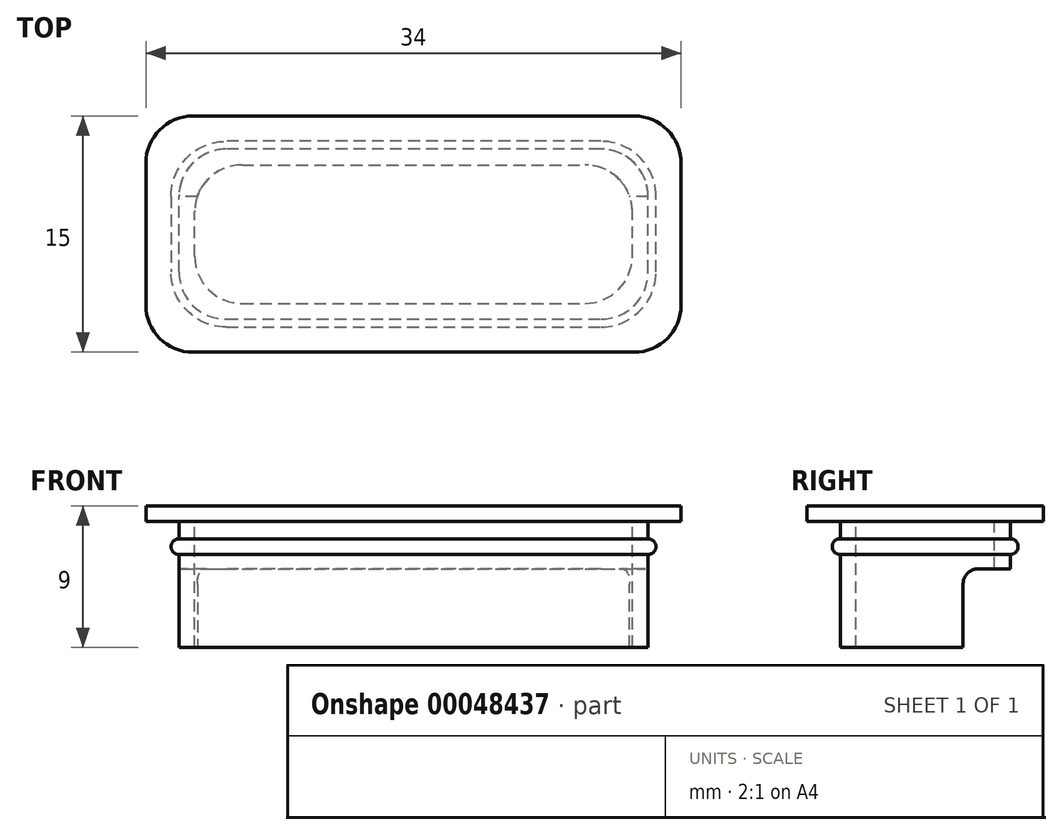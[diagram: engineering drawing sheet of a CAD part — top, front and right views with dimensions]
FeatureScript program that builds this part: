
annotation { "Feature Type Name" : "Feature", "Feature Type Description" : "" }
export const myFeature = defineFeature(function(context is Context, id is Id, definition is map)
    precondition{}
    {
        {
            var Q0;
            Q0=qCreatedBy(makeId("Top.planeOp"),FACE);
            var sketch = newSketch(context, id + "F0", { "sketchPlane" : qUnion([Q0])});
            skLineSegment(sketch, "E0.rect.bottom", {"start": v(17, -7.5) * mm, "end": v(-17, -7.5) * mm});
            skLineSegment(sketch, "E0.rect.top", {"start": v(17, 7.5) * mm, "end": v(-17, 7.5) * mm});
            skLineSegment(sketch, "E0.rect.left", {"start": v(17, -7.5) * mm, "end": v(17, 7.5) * mm});
            skLineSegment(sketch, "E0.rect.right", {"start": v(-17, -7.5) * mm, "end": v(-17, 7.5) * mm});
            skPoint(sketch, "E0.rect.middle", {"position": v(0, 0) * mm});
            skSolve(sketch);
        }
        {
            var Q0;
            Q0=makeQuery(id+"F0.imprint","IMPRINT",FACE,{"disambiguationData":[TD([[makeQuery(id+"F0.imprint","IMPRINT",EDGE,{"derivedFrom":sQuery(id+"F0.wireOp",EDGE,"E0.rect.bottom")}),-1.0]])]});
            extrude(context, id + "F1", {"entities" : qUnion([Q0]), "endBound" : BoundingType.SYMMETRIC, "depth" : 1 * mm});
        }
        {
            var Q0;
            Q0=makeQuery(id+"F1.opExtrude","CAP_FACE",FACE,{"disambiguationData":[OSD([sQuery(id+"F0.wireOp",EDGE,"E0.rect.bottom"),sQuery(id+"F0.wireOp",EDGE,"E0.rect.top"),sQuery(id+"F0.wireOp",EDGE,"E0.rect.left"),sQuery(id+"F0.wireOp",EDGE,"E0.rect.right")])],"isStart":true});
            var sketch = newSketch(context, id + "F2", { "sketchPlane" : qUnion([Q0])});
            skLineSegment(sketch, "E1.rect.bottom", {"start": v(-14.9, 5.4) * mm, "end": v(14.9, 5.4) * mm});
            skLineSegment(sketch, "E1.rect.top", {"start": v(-14.9, -5.4) * mm, "end": v(14.9, -5.4) * mm});
            skLineSegment(sketch, "E1.rect.left", {"start": v(-14.9, 5.4) * mm, "end": v(-14.9, -5.4) * mm});
            skLineSegment(sketch, "E1.rect.right", {"start": v(14.9, 5.4) * mm, "end": v(14.9, -5.4) * mm});
            skPoint(sketch, "E1.rect.middle", {"position": v(0, 0) * mm});
            skSolve(sketch);
        }
        {
            var Q0;
            Q0=makeQuery(id+"F2.imprint","IMPRINT",FACE,{"disambiguationData":[TD([[makeQuery(id+"F2.imprint","IMPRINT",EDGE,{"derivedFrom":sQuery(id+"F2.wireOp",EDGE,"E1.rect.bottom")}),-1.0]])]});
            extrude(context, id + "F3", {"entities" : qUnion([Q0]), "operationType" : NewBodyOperationType.ADD, "depth" : 8 * mm});
        }
        {
            var Q0;
            Q0=makeQuery(id+"F3.opExtrude","CAP_FACE",FACE,{"disambiguationData":[OSD([sQuery(id+"F2.wireOp",EDGE,"E1.rect.bottom"),sQuery(id+"F2.wireOp",EDGE,"E1.rect.top"),sQuery(id+"F2.wireOp",EDGE,"E1.rect.left"),sQuery(id+"F2.wireOp",EDGE,"E1.rect.right")])],"isStart":false});
            shell(context, id + "F4", {"entities" : qUnion([Q0]), "thickness" : 1 * mm});
        }
        {
            var Q0;
            Q0=makeQuery(id+"F1.opExtrude","SWEPT_EDGE",EDGE,{"disambiguationData":[OSD([sQuery(id+"F0.wireOp",EDGE,"E0.rect.bottom"),sQuery(id+"F0.wireOp",EDGE,"E0.rect.right")])]});
            var Q1;
            Q1=makeQuery(id+"F1.opExtrude","SWEPT_EDGE",EDGE,{"disambiguationData":[OSD([sQuery(id+"F0.wireOp",EDGE,"E0.rect.top"),sQuery(id+"F0.wireOp",EDGE,"E0.rect.right")])]});
            var Q2;
            Q2=makeQuery(id+"F1.opExtrude","SWEPT_EDGE",EDGE,{"disambiguationData":[OSD([sQuery(id+"F0.wireOp",EDGE,"E0.rect.top"),sQuery(id+"F0.wireOp",EDGE,"E0.rect.left")])]});
            var Q3;
            Q3=makeQuery(id+"F1.opExtrude","SWEPT_EDGE",EDGE,{"disambiguationData":[OSD([sQuery(id+"F0.wireOp",EDGE,"E0.rect.bottom"),sQuery(id+"F0.wireOp",EDGE,"E0.rect.left")])]});
            var Q4;
            Q4=makeQuery(id+"F3.opExtrude","SWEPT_EDGE",EDGE,{"disambiguationData":[OSD([sQuery(id+"F2.wireOp",EDGE,"E1.rect.top"),sQuery(id+"F2.wireOp",EDGE,"E1.rect.right")])]});
            var Q5;
            Q5=makeQuery(id+"F3.opExtrude","SWEPT_EDGE",EDGE,{"disambiguationData":[OSD([sQuery(id+"F2.wireOp",EDGE,"E1.rect.top"),sQuery(id+"F2.wireOp",EDGE,"E1.rect.left")])]});
            var Q6;
            Q6=makeQuery(id+"F3.opExtrude","SWEPT_EDGE",EDGE,{"disambiguationData":[OSD([sQuery(id+"F2.wireOp",EDGE,"E1.rect.bottom"),sQuery(id+"F2.wireOp",EDGE,"E1.rect.left")])]});
            var Q7;
            Q7=makeQuery(id+"F3.opExtrude","SWEPT_EDGE",EDGE,{"disambiguationData":[OSD([sQuery(id+"F2.wireOp",EDGE,"E1.rect.bottom"),sQuery(id+"F2.wireOp",EDGE,"E1.rect.right")])]});
            var Q8;
            Q8=makeQuery(id+"F4.opShell","OFFSET_EDGE",EDGE,{"disambiguationData":[OSD([sQuery(id+"F2.wireOp",EDGE,"E1.rect.bottom"),sQuery(id+"F2.wireOp",EDGE,"E1.rect.left")])]});
            var Q9;
            Q9=makeQuery(id+"F4.opShell","OFFSET_EDGE",EDGE,{"disambiguationData":[OSD([sQuery(id+"F2.wireOp",EDGE,"E1.rect.top"),sQuery(id+"F2.wireOp",EDGE,"E1.rect.left")])]});
            var Q10;
            Q10=makeQuery(id+"F4.opShell","OFFSET_EDGE",EDGE,{"disambiguationData":[OSD([sQuery(id+"F2.wireOp",EDGE,"E1.rect.top"),sQuery(id+"F2.wireOp",EDGE,"E1.rect.right")])]});
            var Q11;
            Q11=makeQuery(id+"F4.opShell","OFFSET_EDGE",EDGE,{"disambiguationData":[OSD([sQuery(id+"F2.wireOp",EDGE,"E1.rect.bottom"),sQuery(id+"F2.wireOp",EDGE,"E1.rect.right")])]});
            fillet(context, id + "F5", {"entities" : qUnion([Q0, Q1, Q2, Q3, Q4, Q5, Q6, Q7, Q8, Q9, Q10, Q11]), "radius" : 3 * mm, "tangentPropagation" : true, "allowEdgeOverflow" : false});
        }
        {
            var Q0;
            Q0=makeQuery(id+"F1.opExtrude","CAP_FACE",FACE,{"disambiguationData":[OSD([sQuery(id+"F0.wireOp",EDGE,"E0.rect.bottom"),sQuery(id+"F0.wireOp",EDGE,"E0.rect.top"),sQuery(id+"F0.wireOp",EDGE,"E0.rect.left"),sQuery(id+"F0.wireOp",EDGE,"E0.rect.right")])],"isStart":true});
            cPlane(context, id + "F6", {"entities" : qUnion([Q0]), "cplaneType" : CPlaneType.OFFSET, "offset" : 1.1 * mm, "width" : 150 * mm, "height" : 150 * mm});
        }
        {
            var Q0;
            Q0=qCreatedBy(id+"F6.planeOp",FACE);
            var sketch = newSketch(context, id + "F7", { "sketchPlane" : qUnion([Q0])});
            skLineSegment(sketch, "E2.rect.bottom", {"start": v(-11.9, 5.4) * mm, "end": v(11.9, 5.4) * mm});
            skLineSegment(sketch, "E2.rect.top", {"start": v(-11.9, -5.4) * mm, "end": v(11.9, -5.4) * mm});
            skLineSegment(sketch, "E2.rect.left", {"start": v(-14.9, 2.4) * mm, "end": v(-14.9, -2.4) * mm});
            skLineSegment(sketch, "E2.rect.right", {"start": v(14.9, 2.4) * mm, "end": v(14.9, -2.4) * mm});
            skPoint(sketch, "E2.rect.middle", {"position": v(0, 0) * mm});
            skPoint(sketch, "E3.visualSharp", {"position": v(-14.9, -5.4) * mm});
            skArc(sketch, "E3.filletArc", {"start": v(-14.9, -2.4) * mm, "mid": v(-14.02, -4.52) * mm, "end": v(-11.9, -5.4) * mm});
            skPoint(sketch, "E4.visualSharp", {"position": v(-14.9, 5.4) * mm});
            skArc(sketch, "E4.filletArc", {"start": v(-11.9, 5.4) * mm, "mid": v(-14.02, 4.52) * mm, "end": v(-14.9, 2.4) * mm});
            skPoint(sketch, "E5.visualSharp", {"position": v(14.9, 5.4) * mm});
            skArc(sketch, "E5.filletArc", {"start": v(14.9, 2.4) * mm, "mid": v(14.02, 4.52) * mm, "end": v(11.9, 5.4) * mm});
            skPoint(sketch, "E6.visualSharp", {"position": v(14.9, -5.4) * mm});
            skArc(sketch, "E6.filletArc", {"start": v(11.9, -5.4) * mm, "mid": v(14.02, -4.52) * mm, "end": v(14.9, -2.4) * mm});
            skArc(sketch, "E7.0", {"start": v(-15.4, -2.4) * mm, "mid": v(-14.37, -4.87) * mm, "end": v(-11.9, -5.9) * mm});
            skLineSegment(sketch, "E7.1", {"start": v(-15.4, 2.4) * mm, "end": v(-15.4, -2.4) * mm});
            skLineSegment(sketch, "E7.2", {"start": v(-11.9, -5.9) * mm, "end": v(11.9, -5.9) * mm});
            skArc(sketch, "E7.3", {"start": v(-11.9, 5.9) * mm, "mid": v(-14.37, 4.87) * mm, "end": v(-15.4, 2.4) * mm});
            skArc(sketch, "E7.4", {"start": v(11.9, -5.9) * mm, "mid": v(14.37, -4.87) * mm, "end": v(15.4, -2.4) * mm});
            skLineSegment(sketch, "E7.5", {"start": v(15.4, 2.4) * mm, "end": v(15.4, -2.4) * mm});
            skArc(sketch, "E7.6", {"start": v(15.4, 2.4) * mm, "mid": v(14.37, 4.87) * mm, "end": v(11.9, 5.9) * mm});
            skLineSegment(sketch, "E7.7", {"start": v(-11.9, 5.9) * mm, "end": v(11.9, 5.9) * mm});
            skSolve(sketch);
        }
        {
            var Q0;
            Q0=makeQuery(id+"F7.imprint","IMPRINT",FACE,{"disambiguationData":[TD([[makeQuery(id+"F7.imprint","IMPRINT",EDGE,{"derivedFrom":sQuery(id+"F7.wireOp",EDGE,"E2.rect.bottom")}),1.0]])]});
            extrude(context, id + "F8", {"entities" : qUnion([Q0]), "operationType" : NewBodyOperationType.ADD, "depth" : 1 * mm});
        }
        {
            var Q0;
            Q0=makeQuery(id+"F8.opExtrude","CAP_EDGE",EDGE,{"disambiguationData":[OSD([sQuery(id+"F7.wireOp",EDGE,"E7.2")])],"isStart":false});
            var Q1;
            Q1=makeQuery(id+"F8.opExtrude","CAP_EDGE",EDGE,{"disambiguationData":[OSD([sQuery(id+"F7.wireOp",EDGE,"E7.2")])],"isStart":true});
            fillet(context, id + "F9", {"entities" : qUnion([Q0, Q1]), "radius" : .5 * mm, "tangentPropagation" : true, "allowEdgeOverflow" : false});
        }
        {
            var Q0;
            {var subQ0=sQuery(id+"F2.wireOp",EDGE,"E1.rect.top");var subQ1=sQuery(id+"F2.wireOp",EDGE,"E1.rect.right");var subQ2=sQuery(id+"F2.wireOp",EDGE,"E1.rect.left");Q0=makeQuery(id+"F8.boolean.opBoolean","SPLIT",FACE,{"disambiguationData":[TD([makeQuery(id+"F3.opExtrude","CAP_FACE",FACE,{"disambiguationData":[OSD([sQuery(id+"F2.wireOp",EDGE,"E1.rect.bottom"),subQ0,subQ2,subQ1])],"isStart":false})])],"derivedFrom":makeQuery(id+"F3.opExtrude","SWEPT_FACE",FACE,{"disambiguationData":[OSD([subQ0])]})});}
            var sketch = newSketch(context, id + "F10", { "sketchPlane" : qUnion([Q0])});
            skLineSegment(sketch, "E8.bottom", {"start": v(-14.9, -8.5) * mm, "end": v(14.9, -8.5) * mm});
            skLineSegment(sketch, "E8.top", {"start": v(-14.9, -3.5) * mm, "end": v(14.9, -3.5) * mm});
            skLineSegment(sketch, "E8.left", {"start": v(-14.9, -8.5) * mm, "end": v(-14.9, -3.5) * mm});
            skLineSegment(sketch, "E8.right", {"start": v(14.9, -8.5) * mm, "end": v(14.9, -3.5) * mm});
            skSolve(sketch);
        }
        {
            var Q0;
            {var subQ0=sQuery(id+"F10.wireOp",EDGE,"E8.right");Q0=makeQuery(id+"F10.imprint","IMPRINT",FACE,{"disambiguationData":[TD([[makeQuery(id+"F10.imprint","IMPRINT",EDGE,{"derivedFrom":subQ0}),1.0]])]});}
            var Q1;
            {var subQ0=sQuery(id+"F2.wireOp",EDGE,"E1.rect.top");var subQ1=sQuery(id+"F2.wireOp",EDGE,"E1.rect.right");var subQ2=makeQuery(id+"F3.opExtrude","SWEPT_EDGE",EDGE,{"disambiguationData":[OSD([subQ0,subQ1])]});var subQ3=makeQuery(id+"F3.opExtrude","SWEPT_FACE",FACE,{"disambiguationData":[OSD([subQ0])]});var subQ5=sQuery(id+"F2.wireOp",EDGE,"E1.rect.left");var subQ6=makeQuery(id+"F3.opExtrude","CAP_FACE",FACE,{"disambiguationData":[OSD([sQuery(id+"F2.wireOp",EDGE,"E1.rect.bottom"),subQ0,subQ5,subQ1])],"isStart":false});var subQ7=makeQuery(id+"F8.boolean.opBoolean","SPLIT",EDGE,{"disambiguationData":[TD([subQ6])],"derivedFrom":makeQuery(id+"F5.opFillet","BLEND_EDGE",EDGE,{"blendedFrom":[subQ2,subQ3],"blendedInto":[subQ3]})});var subQ10=sQuery(id+"F10.wireOp",EDGE,"E8.bottom");var subQ11=makeQuery(id+"F10.imprint","INTERSECT",VERTEX,{"derivedFrom":[subQ7,subQ10]});var subQ12=makeQuery(id+"F3.opExtrude","SWEPT_EDGE",EDGE,{"disambiguationData":[OSD([subQ0,subQ5])]});var subQ13=makeQuery(id+"F8.boolean.opBoolean","SPLIT",EDGE,{"disambiguationData":[TD([subQ6])],"derivedFrom":makeQuery(id+"F5.opFillet","BLEND_EDGE",EDGE,{"blendedFrom":[subQ12,subQ3],"blendedInto":[subQ3]})});var subQ15=makeQuery(id+"F10.imprint","INTERSECT",VERTEX,{"derivedFrom":[subQ13,subQ10]});Q1=makeQuery(id+"F10.imprint","IMPRINT",FACE,{"disambiguationData":[TD([[makeQuery(id+"F10.imprint","IMPRINT",EDGE,{"disambiguationData":[TD([[subQ15,-1.0],[subQ11,1.0]])],"derivedFrom":subQ10}),-1.0]])]});}
            var Q2;
            {var subQ9=sQuery(id+"F10.wireOp",EDGE,"E8.left");Q2=makeQuery(id+"F10.imprint","IMPRINT",FACE,{"disambiguationData":[TD([[makeQuery(id+"F10.imprint","IMPRINT",EDGE,{"derivedFrom":subQ9}),-1.0]])]});}
            extrude(context, id + "F12", {"entities" : qUnion([Q0, Q1, Q2]), "operationType" : NewBodyOperationType.REMOVE, "oppositeDirection" : true, "depth" : 3 * mm});
        }
        {
            var Q0;
            Q0=makeQuery(id+"F12.boolean.opBoolean","COPY",EDGE,{"disambiguationData":[OD(0.0)],"derivedFrom":makeQuery(id+"F12.opExtrude","CAP_EDGE",EDGE,{"disambiguationData":[OSD([sQuery(id+"F10.wireOp",EDGE,"E8.bottom")])],"isStart":false})});
            var Q1;
            Q1=makeQuery(id+"F12.boolean.opBoolean","COPY",EDGE,{"disambiguationData":[OD(1.0)],"derivedFrom":makeQuery(id+"F12.opExtrude","CAP_EDGE",EDGE,{"disambiguationData":[OSD([sQuery(id+"F10.wireOp",EDGE,"E8.top")])],"isStart":false})});
            var Q2;
            Q2=makeQuery(id+"F12.boolean.opBoolean","COPY",EDGE,{"disambiguationData":[OD(0.0)],"derivedFrom":makeQuery(id+"F12.opExtrude","CAP_EDGE",EDGE,{"disambiguationData":[OSD([sQuery(id+"F10.wireOp",EDGE,"E8.top")])],"isStart":false})});
            var Q3;
            Q3=makeQuery(id+"F12.boolean.opBoolean","COPY",EDGE,{"disambiguationData":[OD(1.0)],"derivedFrom":makeQuery(id+"F12.opExtrude","CAP_EDGE",EDGE,{"disambiguationData":[OSD([sQuery(id+"F10.wireOp",EDGE,"E8.bottom")])],"isStart":false})});
            fillet(context, id + "F11", {"entities" : qUnion([Q0, Q1, Q2, Q3]), "radius" : 1 * mm, "tangentPropagation" : true, "allowEdgeOverflow" : false});
        }
    });
